# Revit family: S-69 (EN)
name_source: partatom
category: Pipe Fittings
revit_build: Autodesk Revit 2015 (Build: 20140606_1530(x64)
units: mm (PartAtom-declared; Revit-internal decimal feet)

## types (2) — shared parameters
Appliances = WASH BASIN, BIDET
Certificates = http://www.jimten.com
Description = BOTTLE TRAP COMPACT, EXTENSIBLE, HORIZONTAL OUTLET,  JUNTA FIX RAISER
Flowrate = 0.4 L/s
Manufacturer = Jimten
Material = PP (White)
Model = S-69
Type Comments = EASY INSTALLATION THANKS TO ITS INTEGRATED JOINT SYSTEMS, BOTTOM REGISTER COVER
URL = http://www.jimten.com

## per-type parameters (varying)
| type | AMax | AMin | B | DiameterInlet | DiameterOutlet | Inlets | Outlet | Reference |
| S-69_1 1/2" | 220 mm  [stored 0.721785 ft] | 150 mm | 60 mm  [stored 0.19685 ft] | 38 mm | 40 mm  [stored 0.131234 ft] | 1 1/2" FEMALE THREAD | Ø40 MM (FEMALE) | 04058 |
| S-69_1 1/4" | 205 mm  [stored 0.672572 ft] | 140 mm  [stored 0.459318 ft] | 50 mm  [stored 0.164042 ft] | 32 mm  [stored 0.104987 ft] | 32 mm  [stored 0.104987 ft] | 1 1/4" FEMALE THREAD | Ø32 MM (FEMALE) | 04016 |

note: [stored X ft] marks values corroborated as IEEE doubles in the binary element streams (Revit-internal decimal feet)

## geometry (parser evidence)
native form markers: Blend x2
no freeform markers — native parametric forms only
